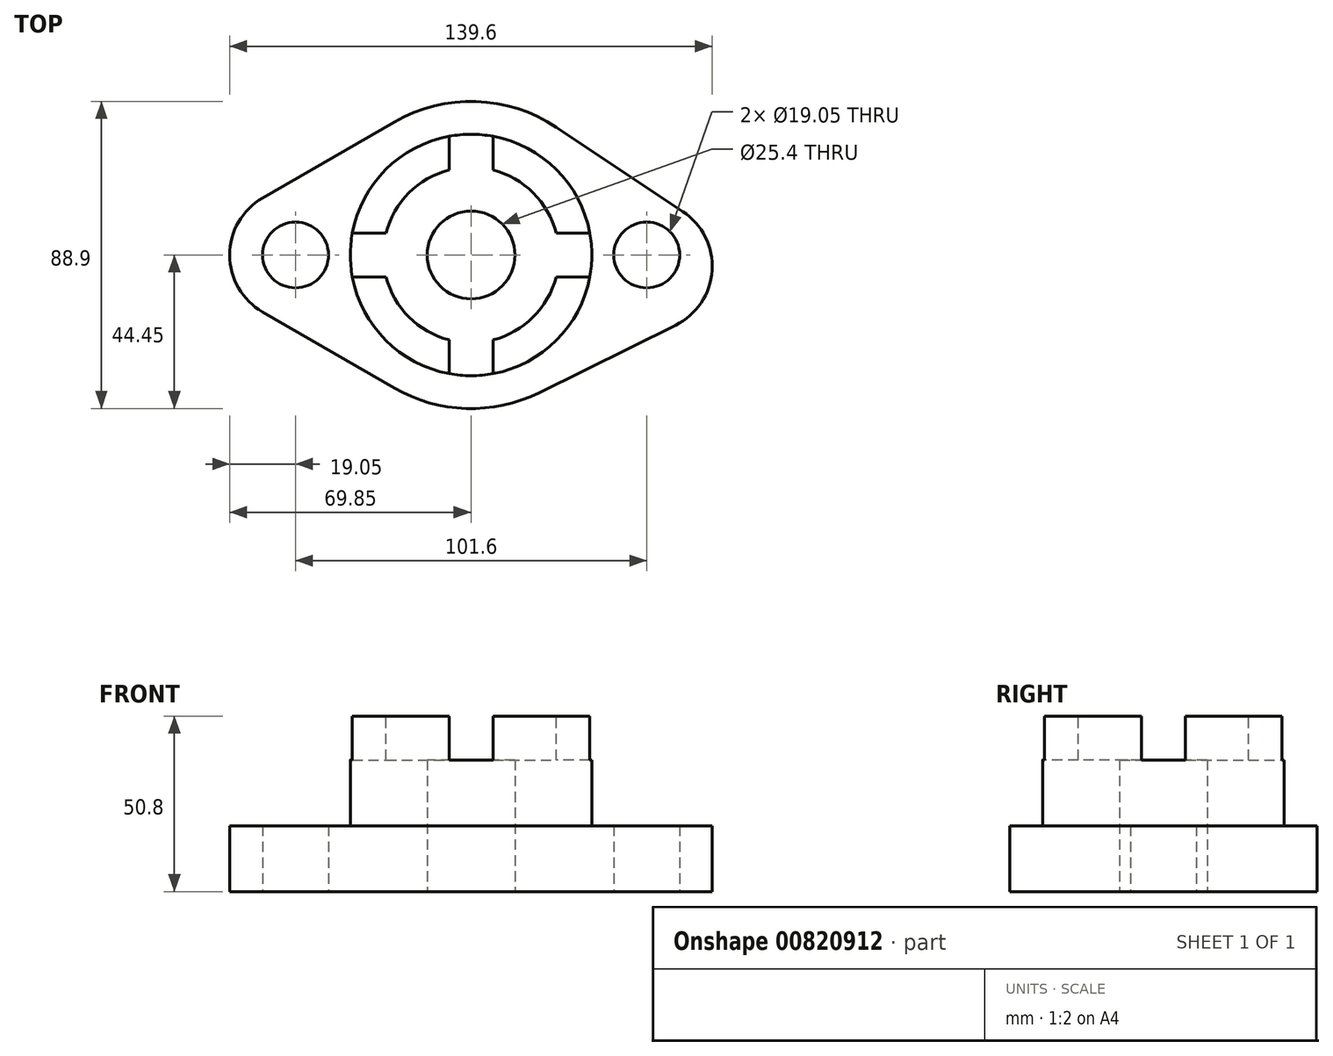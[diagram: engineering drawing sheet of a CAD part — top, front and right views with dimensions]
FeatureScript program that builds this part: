
annotation { "Feature Type Name" : "Feature", "Feature Type Description" : "" }
export const myFeature = defineFeature(function(context is Context, id is Id, definition is map)
    precondition{}
    {
        {
            var Q0;
            Q0=qCreatedBy(makeId("Top.planeOp"),FACE);
            var sketch = newSketch(context, id + "F0", { "sketchPlane" : qUnion([Q0])});
            skCircle(sketch, "E0", {"center": v(0, 0) * mm, "radius": 12.7 * mm});
            skCircle(sketch, "E1", {"center": v(0, 0) * mm, "radius": 25.4 * mm});
            skCircle(sketch, "E2", {"center": v(0, 0) * mm, "radius": 34.93 * mm});
            skCircle(sketch, "E3", {"center": v(-50.8, 0) * mm, "radius": 9.53 * mm});
            skCircle(sketch, "E4", {"center": v(50.8, 0) * mm, "radius": 9.53 * mm});
            skPoint(sketch, "E5.start.orphan", {"position": v(0, 46.83) * mm});
            skPoint(sketch, "E6.start.orphan", {"position": v(100.25, 0) * mm});
            skPoint(sketch, "E7.end.orphan", {"position": v(-88.9, 0) * mm});
            skPoint(sketch, "E7.start.orphan", {"position": v(0, -48.27) * mm});
            skArc(sketch, "E8", {"start": v(-22.22, -38.5) * mm, "mid": v(-1.43, -44.43) * mm, "end": v(19.7, -39.84) * mm});
            skArc(sketch, "E9", {"start": v(-22.22, 38.5) * mm, "mid": v(1.43, 44.43) * mm, "end": v(24.65, 36.99) * mm});
            skLineSegment(sketch, "E10", {"start": v(-22.22, 38.5) * mm, "end": v(-60.33, 16.5) * mm});
            skLineSegment(sketch, "E11", {"start": v(-60.33, -16.5) * mm, "end": v(-22.22, -38.5) * mm});
            skLineSegment(sketch, "E12", {"start": v(19.7, -39.84) * mm, "end": v(59.14, -20.34) * mm});
            skArc(sketch, "E13.filletArc", {"start": v(-60.33, 16.5) * mm, "mid": v(-69.85, 0) * mm, "end": v(-60.33, -16.5) * mm});
            skArc(sketch, "E14.filletArc", {"start": v(59.14, -20.34) * mm, "mid": v(69.7, -4.48) * mm, "end": v(61.26, 12.6) * mm});
            skLineSegment(sketch, "E15", {"start": v(24.65, 36.99) * mm, "end": v(61.26, 12.6) * mm});
            skSolve(sketch);
        }
        {
            var Q0;
            Q0=makeQuery(id+"F0.imprint","IMPRINT",FACE,{"disambiguationData":[TD([[makeQuery(id+"F0.imprint","IMPRINT",EDGE,{"derivedFrom":sQuery(id+"F0.wireOp",EDGE,"E2")}),-1.0]])]});
            extrude(context, id + "F1", {"entities" : qUnion([Q0]), "depth" : 19.05 * mm, "offsetDistance" : 25.4 * mm});
        }
        {
            var Q0;
            Q0=makeQuery(id+"F0.imprint","IMPRINT",FACE,{"disambiguationData":[TD([[makeQuery(id+"F0.imprint","IMPRINT",EDGE,{"derivedFrom":sQuery(id+"F0.wireOp",EDGE,"E1")}),-1.0]])]});
            extrude(context, id + "F2", {"entities" : qUnion([Q0]), "operationType" : NewBodyOperationType.ADD, "depth" : 50.8 * mm, "offsetDistance" : 25.4 * mm});
        }
        {
            var Q0;
            Q0=makeQuery(id+"F0.imprint","IMPRINT",FACE,{"disambiguationData":[TD([[makeQuery(id+"F0.imprint","IMPRINT",EDGE,{"derivedFrom":sQuery(id+"F0.wireOp",EDGE,"E0")}),-1.0]])]});
            extrude(context, id + "F3", {"entities" : qUnion([Q0]), "operationType" : NewBodyOperationType.ADD, "depth" : 38.1 * mm, "offsetDistance" : 25.4 * mm});
        }
        {
            var Q0;
            Q0=makeQuery(id+"F2.opExtrude","CAP_FACE",FACE,{"disambiguationData":[OSD([sQuery(id+"F0.wireOp",EDGE,"E1"),sQuery(id+"F0.wireOp",EDGE,"E2")])],"isStart":false});
            var sketch = newSketch(context, id + "F4", { "sketchPlane" : qUnion([Q0])});
            skLineSegment(sketch, "E16", {"start": v(-6.35, 34.34) * mm, "end": v(-6.35, 24.6) * mm});
            skLineSegment(sketch, "E17", {"start": v(6.35, 24.6) * mm, "end": v(6.35, 34.34) * mm});
            skPoint(sketch, "E18.1.internal.orphan", {"position": v(0, 26.2) * mm});
            skPoint(sketch, "E19.1.internal.orphan", {"position": v(0, 35.5) * mm});
            skSolve(sketch);
        }
        {
            var Q0;
            {var subQ0=sQuery(id+"F4.wireOp",EDGE,"E16");Q0=makeQuery(id+"F4.imprint","IMPRINT",FACE,{"disambiguationData":[TD([[makeQuery(id+"F4.imprint","IMPRINT",EDGE,{"derivedFrom":subQ0}),1.0]])]});}
            extrude(context, id + "F5", {"entities" : qUnion([Q0]), "operationType" : NewBodyOperationType.REMOVE, "oppositeDirection" : true, "depth" : 12.7 * mm, "offsetDistance" : 25.4 * mm});
        }
        {
            var Q0;
            Q0=makeQuery(id+"F2.opExtrude","CAP_FACE",FACE,{"disambiguationData":[OSD([sQuery(id+"F0.wireOp",EDGE,"E1"),sQuery(id+"F0.wireOp",EDGE,"E2")])],"isStart":false});
            var sketch = newSketch(context, id + "F6", { "sketchPlane" : qUnion([Q0])});
            skLineSegment(sketch, "E20", {"start": v(-34.34, 6.35) * mm, "end": v(-24.6, 6.35) * mm});
            skLineSegment(sketch, "E21", {"start": v(-34.34, -6.35) * mm, "end": v(-24.6, -6.35) * mm});
            skLineSegment(sketch, "E22", {"start": v(-6.35, -24.6) * mm, "end": v(-6.35, -34.34) * mm});
            skLineSegment(sketch, "E23", {"start": v(6.35, -34.34) * mm, "end": v(6.35, -24.6) * mm});
            skLineSegment(sketch, "E24", {"start": v(24.6, 6.35) * mm, "end": v(34.34, 6.35) * mm});
            skLineSegment(sketch, "E25", {"start": v(34.34, -6.35) * mm, "end": v(24.6, -6.35) * mm});
            skPoint(sketch, "E26.start.orphan", {"position": v(-36.47, -6.35) * mm});
            skSolve(sketch);
        }
        {
            var Q0;
            {var subQ0=sQuery(id+"F6.wireOp",EDGE,"E21");Q0=makeQuery(id+"F6.imprint","IMPRINT",FACE,{"disambiguationData":[TD([[makeQuery(id+"F6.imprint","IMPRINT",EDGE,{"derivedFrom":subQ0}),1.0]])]});}
            var Q1;
            {var subQ0=sQuery(id+"F6.wireOp",EDGE,"E22");Q1=makeQuery(id+"F6.imprint","IMPRINT",FACE,{"disambiguationData":[TD([[makeQuery(id+"F6.imprint","IMPRINT",EDGE,{"derivedFrom":subQ0}),1.0]])]});}
            var Q2;
            {var subQ0=sQuery(id+"F6.wireOp",EDGE,"E24");Q2=makeQuery(id+"F6.imprint","IMPRINT",FACE,{"disambiguationData":[TD([[makeQuery(id+"F6.imprint","IMPRINT",EDGE,{"derivedFrom":subQ0}),-1.0]])]});}
            extrude(context, id + "F7", {"entities" : qUnion([Q0, Q1, Q2]), "operationType" : NewBodyOperationType.REMOVE, "oppositeDirection" : true, "depth" : 12.7 * mm, "offsetDistance" : 25.4 * mm});
        }
    });
